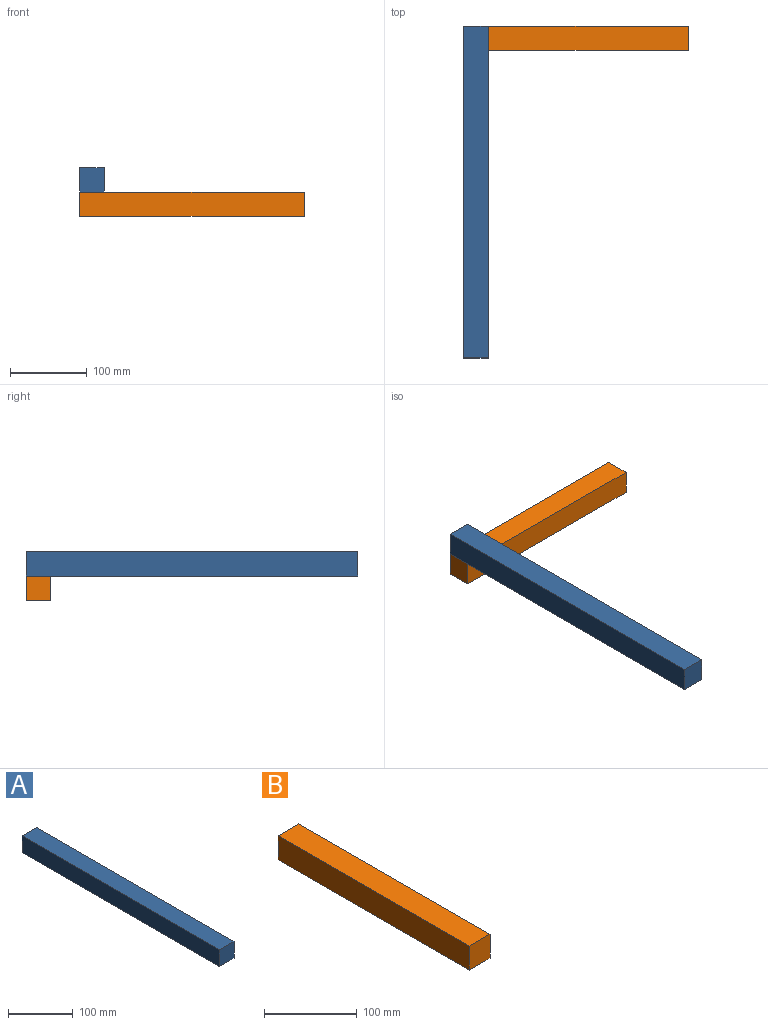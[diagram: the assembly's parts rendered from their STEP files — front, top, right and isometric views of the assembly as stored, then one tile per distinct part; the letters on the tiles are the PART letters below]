
ASSEMBLY  parts=2 mates=1
PART A: 6 faces, bbox 31.8x431.8x31.8 mm
  f0: plane 431.8x31.75mm, normal (1,0,0), area 13709.6mm2, adj f1,f3,f4,f5
  f1: plane 431.8x31.75mm, normal (0,0,1), area 13709.6mm2, adj f0,f2,f4,f5
  f2: plane 431.8x31.75mm, normal (-1,0,0), area 13709.6mm2, adj f1,f3,f4,f5
  f3: plane 431.8x31.75mm, normal (0,0,-1), area 13709.6mm2, adj f0,f2,f4,f5
  f4: plane 31.75x31.75mm, normal (0,-1,0), area 1008.1mm2, adj f0,f1,f2,f3
  f5: plane 31.75x31.75mm, normal (0,1,0), area 1008.1mm2, adj f0,f1,f2,f3
PART B: 6 faces, bbox 31.8x292.1x31.8 mm
  f0: plane 292.1x31.75mm, normal (1,0,0), area 9274.2mm2, adj f1,f3,f4,f5
  f1: plane 292.1x31.75mm, normal (0,0,1), area 9274.2mm2, adj f0,f2,f4,f5
  f2: plane 292.1x31.75mm, normal (-1,0,0), area 9274.2mm2, adj f1,f3,f4,f5
  f3: plane 292.1x31.75mm, normal (0,0,-1), area 9274.2mm2, adj f0,f2,f4,f5
  f4: plane 31.75x31.75mm, normal (0,-1,0), area 1008.1mm2, adj f0,f1,f2,f3
  f5: plane 31.75x31.75mm, normal (0,1,0), area 1008.1mm2, adj f0,f1,f2,f3
PLACE A t=(84.27,40.4,-12.38)mm
PLACE B rot(axis=(0.71,-0.71,0),180deg) t=(68.4,24.53,-44.13)mm
MATE fastened B.f3 <-> A.f3  axis (0,0,1) through (84.27,24.53,-28.25)mm
